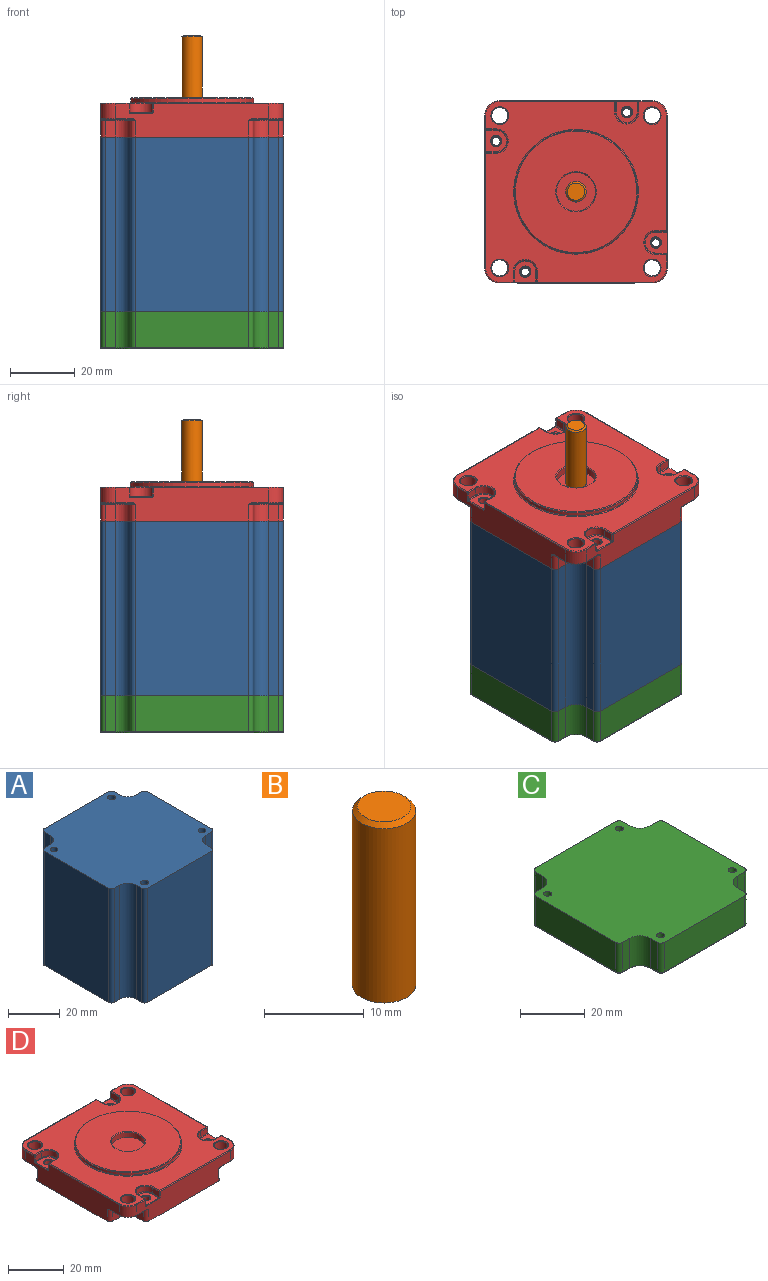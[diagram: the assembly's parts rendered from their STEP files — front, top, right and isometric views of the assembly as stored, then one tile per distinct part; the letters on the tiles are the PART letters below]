
ASSEMBLY  parts=4 mates=3
PART A: 30 faces, bbox 56.4x56.4x54 mm
  f0: cylinder r=1.5mm len=54mm, axis (0,0,1), area 508.9mm2, adj f8,f9
  f1: cylinder r=1.5mm len=54mm, axis (0,0,1), area 508.9mm2, adj f8,f9
  f2: cylinder r=1.5mm len=54mm, axis (0,0,1), area 508.9mm2, adj f8,f9
  f3: cylinder r=1.5mm len=54mm, axis (0,0,1), area 508.9mm2, adj f8,f9
  f4: plane 54x35.14mm, normal (0,-1,0), area 1897.6mm2, adj f8,f9,f25,f26
  f5: plane 54x35.14mm, normal (-1,0,0), area 1897.6mm2, adj f8,f9,f23,f24
  f6: plane 54x35.14mm, normal (0,1,0), area 1897.6mm2, adj f8,f9,f22,f29
  f7: plane 54x35.14mm, normal (1,0,0), area 1897.6mm2, adj f8,f9,f27,f28
  f8: plane 56.4x56.4mm, normal (0,0,-1), area 2832.8mm2, adj f0,f1,f2,f3,f4,f5,f6,f7
  f9: plane 56.4x56.4mm, normal (0,0,1), area 2832.8mm2, adj f0,f1,f2,f3,f4,f5,f6,f7
  f10: plane 54x3.13mm, normal (0,1,0), area 169mm2, adj f8,f9,f12,f28
  f11: plane 54x3.13mm, normal (1,0,0), area 169mm2, adj f8,f9,f12,f29
  f12: cylinder r=4.5mm len=54mm, axis (0,0,1), area 381.7mm2, adj f8,f9,f10,f11
  f13: plane 54x3.13mm, normal (-1,0,0), area 169mm2, adj f8,f9,f14,f22
  f14: cylinder r=4.5mm len=54mm, axis (0,0,1), area 381.7mm2, adj f8,f9,f13,f15
  f15: plane 54x3.13mm, normal (0,1,0), area 169mm2, adj f8,f9,f14,f23
  f16: plane 54x3.13mm, normal (0,-1,0), area 169mm2, adj f8,f9,f17,f24
  f17: cylinder r=4.5mm len=54mm, axis (0,0,1), area 381.7mm2, adj f8,f9,f16,f18
  f18: plane 54x3.13mm, normal (-1,0,0), area 169mm2, adj f8,f9,f17,f25
  f19: cylinder r=4.5mm len=54mm, axis (0,0,1), area 381.7mm2, adj f8,f9,f20,f21
  f20: plane 54x3.13mm, normal (0,-1,0), area 169mm2, adj f8,f9,f19,f27
  f21: plane 54x3.13mm, normal (1,0,0), area 169mm2, adj f8,f9,f19,f26
  f22: cylinder r=1.5mm len=54mm, axis (0,0,1), area 127.2mm2, adj f6,f8,f9,f13
  f23: cylinder r=1.5mm len=54mm, axis (0,0,-1), area 127.2mm2, adj f5,f8,f9,f15
  f24: cylinder r=1.5mm len=54mm, axis (0,0,1), area 127.2mm2, adj f5,f8,f9,f16
  f25: cylinder r=1.5mm len=54mm, axis (0,0,-1), area 127.2mm2, adj f4,f8,f9,f18
  f26: cylinder r=1.5mm len=54mm, axis (0,0,1), area 127.2mm2, adj f4,f8,f9,f21
  f27: cylinder r=1.5mm len=54mm, axis (0,0,-1), area 127.2mm2, adj f7,f8,f9,f20
  f28: cylinder r=1.5mm len=54mm, axis (0,0,1), area 127.2mm2, adj f7,f8,f9,f10
  f29: cylinder r=1.5mm len=54mm, axis (0,0,-1), area 127.2mm2, adj f6,f8,f9,f11
PART B: 4 faces, bbox 6.4x6.4x21.9 mm
  f0: cone r=2.67mm half-angle=45deg, axis (0,0,-1), area 13mm2, adj f1,f2
  f1: cylinder r=3.17mm len=21.4mm, axis (0,0,-1), area 426.9mm2, adj f0,f3
  f2: plane 5.35x5.35mm, normal (0,0,1), area 22.5mm2, adj f0
  f3: plane 6.35x6.35mm, normal (0,0,-1), area 31.7mm2, adj f1
PART C: 61 faces, bbox 56.6x56.6x11.5 mm
  f0: cone r=6mm half-angle=45deg, axis (0,0,-1), area 13.6mm2, adj f9,f14
  f1: cone r=1.25mm half-angle=45deg, axis (0,0,-1), area 6.7mm2, adj f2,f14
  f2: cylinder r=1.25mm len=11mm, axis (0,0,1), area 86.4mm2, adj f1,f15
  f3: cone r=1.25mm half-angle=45deg, axis (0,0,-1), area 6.7mm2, adj f4,f14
  f4: cylinder r=1.25mm len=11mm, axis (0,0,1), area 86.4mm2, adj f3,f15
  f5: cone r=1.25mm half-angle=45deg, axis (0,0,-1), area 6.7mm2, adj f6,f14
  f6: cylinder r=1.25mm len=11mm, axis (0,0,1), area 86.4mm2, adj f5,f15
  f7: cone r=1.25mm half-angle=45deg, axis (0,0,-1), area 6.7mm2, adj f8,f14
  f8: cylinder r=1.25mm len=11mm, axis (0,0,1), area 86.4mm2, adj f7,f15
  f9: cylinder r=6mm len=12mm, axis (0,0,-1), area 141.4mm2, adj f0,f16
  f10: plane 35.14x11.25mm, normal (1,0,0), area 395.3mm2, adj f15,f34,f35,f56
  f11: plane 35.14x11.25mm, normal (0,-1,0), area 395.3mm2, adj f15,f32,f33,f44
  f12: plane 35.14x11.25mm, normal (-1,0,0), area 395.3mm2, adj f15,f30,f31,f41
  f13: plane 35.14x11.25mm, normal (0,1,0), area 395.3mm2, adj f15,f29,f36,f53
  f14: plane 55.9x55.9mm, normal (0,0,-1), area 2646.9mm2, adj f0,f1,f3,f5,f7,f37,f38,f39
  f15: plane 56.4x56.4mm, normal (0,0,1), area 2841.4mm2, adj f2,f4,f6,f8,f10,f11,f12,f13
  f16: plane 12x12mm, normal (0,0,-1), area 113.1mm2, adj f9
  f17: plane 11.25x3.13mm, normal (0,1,0), area 35.2mm2, adj f15,f19,f35,f60
  f18: plane 11.25x3.13mm, normal (1,0,0), area 35.2mm2, adj f15,f19,f36,f57
  f19: cylinder r=4.5mm len=11.25mm, axis (0,0,1), area 79.5mm2, adj f15,f17,f18,f59
  f20: plane 11.25x3.13mm, normal (-1,0,0), area 35.2mm2, adj f15,f21,f29,f49
  f21: cylinder r=4.5mm len=11.25mm, axis (0,0,1), area 79.5mm2, adj f15,f20,f22,f47
  f22: plane 11.25x3.13mm, normal (0,1,0), area 35.2mm2, adj f15,f21,f30,f45
  f23: plane 11.25x3.13mm, normal (0,-1,0), area 35.2mm2, adj f15,f24,f31,f37
  f24: cylinder r=4.5mm len=11.25mm, axis (0,0,1), area 79.5mm2, adj f15,f23,f25,f38
  f25: plane 11.25x3.13mm, normal (-1,0,0), area 35.2mm2, adj f15,f24,f32,f40
  f26: plane 11.25x3.13mm, normal (0,-1,0), area 35.2mm2, adj f15,f27,f34,f52
  f27: cylinder r=4.5mm len=11.25mm, axis (0,0,1), area 79.5mm2, adj f15,f26,f28,f50
  f28: plane 11.25x3.13mm, normal (1,0,0), area 35.2mm2, adj f15,f27,f33,f48
  f29: cylinder r=1.5mm len=11.25mm, axis (0,0,1), area 26.5mm2, adj f13,f15,f20,f51
  f30: cylinder r=1.5mm len=11.25mm, axis (0,0,-1), area 26.5mm2, adj f12,f15,f22,f43
  f31: cylinder r=1.5mm len=11.25mm, axis (0,0,1), area 26.5mm2, adj f12,f15,f23,f39
  f32: cylinder r=1.5mm len=11.25mm, axis (0,0,-1), area 26.5mm2, adj f11,f15,f25,f42
  f33: cylinder r=1.5mm len=11.25mm, axis (0,0,1), area 26.5mm2, adj f11,f15,f28,f46
  f34: cylinder r=1.5mm len=11.25mm, axis (0,0,-1), area 26.5mm2, adj f10,f15,f26,f54
  f35: cylinder r=1.5mm len=11.25mm, axis (0,0,1), area 26.5mm2, adj f10,f15,f17,f58
  f36: cylinder r=1.5mm len=11.25mm, axis (0,0,-1), area 26.5mm2, adj f13,f15,f18,f55
  f37: cylinder r=0.25mm len=3.13mm, axis (1,0,0), area 1.2mm2, adj f14,f23,f38,f39
  f38: torus R=4.75mm, axis (0,0,-1), area 2.8mm2, adj f14,f24,f37,f40
  f39: torus R=1.25mm, axis (0,0,-1), area 0.9mm2, adj f14,f31,f37,f41
  f40: cylinder r=0.25mm len=3.13mm, axis (0,-1,0), area 1.2mm2, adj f14,f25,f38,f42
  f41: cylinder r=0.25mm len=35.14mm, axis (0,-1,0), area 13.8mm2, adj f12,f14,f39,f43
  f42: torus R=1.25mm, axis (0,0,-1), area 0.9mm2, adj f14,f32,f40,f44
  f43: torus R=1.25mm, axis (0,0,-1), area 0.9mm2, adj f14,f30,f41,f45
  f44: cylinder r=0.25mm len=35.14mm, axis (1,0,0), area 13.8mm2, adj f11,f14,f42,f46
  f45: cylinder r=0.25mm len=3.13mm, axis (-1,0,0), area 1.2mm2, adj f14,f22,f43,f47
  f46: torus R=1.25mm, axis (0,0,-1), area 0.9mm2, adj f14,f33,f44,f48
  f47: torus R=4.75mm, axis (0,0,-1), area 2.8mm2, adj f14,f21,f45,f49
  f48: cylinder r=0.25mm len=3.13mm, axis (0,1,0), area 1.2mm2, adj f14,f28,f46,f50
  f49: cylinder r=0.25mm len=3.13mm, axis (0,-1,0), area 1.2mm2, adj f14,f20,f47,f51
  f50: torus R=4.75mm, axis (0,0,-1), area 2.8mm2, adj f14,f27,f48,f52
  f51: torus R=1.25mm, axis (0,0,-1), area 0.9mm2, adj f14,f29,f49,f53
  f52: cylinder r=0.25mm len=3.13mm, axis (1,0,0), area 1.2mm2, adj f14,f26,f50,f54
  f53: cylinder r=0.25mm len=35.14mm, axis (-1,0,0), area 13.8mm2, adj f13,f14,f51,f55
  f54: torus R=1.25mm, axis (0,0,-1), area 0.9mm2, adj f14,f34,f52,f56
  f55: torus R=1.25mm, axis (0,0,-1), area 0.9mm2, adj f14,f36,f53,f57
  f56: cylinder r=0.25mm len=35.14mm, axis (0,1,0), area 13.8mm2, adj f10,f14,f54,f58
  f57: cylinder r=0.25mm len=3.13mm, axis (0,1,0), area 1.2mm2, adj f14,f18,f55,f59
  f58: torus R=1.25mm, axis (0,0,-1), area 0.9mm2, adj f14,f35,f56,f60
  f59: torus R=4.75mm, axis (0,0,-1), area 2.8mm2, adj f14,f19,f57,f60
  f60: cylinder r=0.25mm len=3.13mm, axis (-1,0,0), area 1.2mm2, adj f14,f17,f58,f59
PART D: 174 faces, bbox 57.8x57.8x12.3 mm
  f0: cone r=6mm half-angle=45deg, axis (0,0,1), area 13.6mm2, adj f26,f34
  f1: cone r=18.8mm half-angle=45deg, axis (0,0,-1), area 42mm2, adj f27,f34
  f2: torus R=19.3mm, axis (0,0,1), area 47.2mm2, adj f27,f33
  f3: torus R=2.75mm, axis (0,0,1), area 6.4mm2, adj f18,f55
  f4: torus R=2.75mm, axis (0,0,1), area 6.4mm2, adj f20,f63
  f5: torus R=2.75mm, axis (0,0,1), area 6.4mm2, adj f24,f59
  f6: torus R=2.75mm, axis (0,0,1), area 6.4mm2, adj f22,f68
  f7: torus R=3.75mm, axis (0,0,1), area 4.4mm2, adj f25,f33,f98,f104
  f8: torus R=3.25mm, axis (0,0,1), area 4.2mm2, adj f25,f38,f85,f97
  f9: cone r=1.75mm half-angle=45deg, axis (0,0,1), area 3.6mm2, adj f10,f50
  f10: cylinder r=1.5mm len=7.25mm, axis (0,0,1), area 68.3mm2, adj f9,f32
  f11: cone r=1.75mm half-angle=45deg, axis (0,0,1), area 3.6mm2, adj f12,f38
  f12: cylinder r=1.5mm len=7.25mm, axis (0,0,1), area 68.3mm2, adj f11,f32
  f13: cone r=1.75mm half-angle=45deg, axis (0,0,1), area 3.6mm2, adj f14,f42
  f14: cylinder r=1.5mm len=7.25mm, axis (0,0,1), area 68.3mm2, adj f13,f32
  f15: cone r=1.75mm half-angle=45deg, axis (0,0,1), area 3.6mm2, adj f16,f46
  f16: cylinder r=1.5mm len=7.25mm, axis (0,0,1), area 68.3mm2, adj f15,f32
  f17: cone r=2.75mm half-angle=45deg, axis (0,0,1), area 5.8mm2, adj f18,f33
  f18: cylinder r=2.5mm len=5mm, axis (0,0,1), area 70.7mm2, adj f3,f17
  f19: cone r=2.75mm half-angle=45deg, axis (0,0,1), area 5.8mm2, adj f20,f33
  f20: cylinder r=2.5mm len=5mm, axis (0,0,1), area 70.7mm2, adj f4,f19
  f21: cone r=2.75mm half-angle=45deg, axis (0,0,1), area 5.8mm2, adj f22,f33
  f22: cylinder r=2.5mm len=5mm, axis (0,0,1), area 70.7mm2, adj f6,f21
  f23: cone r=2.75mm half-angle=45deg, axis (0,0,1), area 5.8mm2, adj f24,f33
  f24: cylinder r=2.5mm len=5mm, axis (0,0,1), area 70.7mm2, adj f5,f23
  f25: cylinder r=3.5mm len=7mm, axis (0,0,1), area 27.5mm2, adj f7,f8,f36,f37
  f26: cylinder r=6mm len=12mm, axis (0,0,1), area 84.8mm2, adj f0,f35
  f27: cylinder r=19.05mm len=38.1mm, axis (0,0,-1), area 131.7mm2, adj f1,f2
  f28: plane 47.61x10.46mm, normal (1,0,0), area 396.6mm2, adj f32,f44,f45,f46,f53,f54,f76,f77
  f29: plane 47.61x10.46mm, normal (0,-1,0), area 393.4mm2, adj f32,f51,f53,f74,f75,f112,f116,f120
  f30: plane 47.61x10.46mm, normal (-1,0,0), area 393.4mm2, adj f32,f51,f52,f72,f73,f87,f88,f92
  f31: plane 47.61x10.46mm, normal (0,1,0), area 393.4mm2, adj f32,f52,f54,f71,f78,f80,f81,f86
  f32: plane 56.4x56.4mm, normal (0,0,-1), area 2832.8mm2, adj f10,f12,f14,f16,f28,f29,f30,f31
  f33: plane 55.9x55.9mm, normal (0,0,1), area 1658.2mm2, adj f2,f7,f17,f19,f21,f23,f80,f82
  f34: plane 37.6x37.6mm, normal (0,0,1), area 987.6mm2, adj f0,f1
  f35: plane 12x12mm, normal (0,0,1), area 113.1mm2, adj f26
  f36: plane 3.25x2.5mm, normal (0,1,0), area 8.1mm2, adj f25,f97,f103,f104
  f37: plane 3.25x2.5mm, normal (0,-1,0), area 8.1mm2, adj f25,f85,f87,f98
  f38: plane 6.5x6.5mm, normal (0,0,1), area 28.1mm2, adj f8,f11,f85,f96,f97
  f39: cylinder r=3.5mm len=7mm, axis (0,0,1), area 27.5mm2, adj f40,f41,f121,f122
  f40: plane 3.25x2.5mm, normal (-1,0,0), area 8.1mm2, adj f39,f125,f126,f130
  f41: plane 3.25x2.5mm, normal (1,0,0), area 8.1mm2, adj f39,f116,f117,f118
  f42: plane 6.5x6.5mm, normal (0,0,1), area 28.1mm2, adj f13,f117,f121,f124,f125
  f43: cylinder r=3.5mm len=7mm, axis (0,0,1), area 27.5mm2, adj f44,f45,f113,f132
  f44: plane 3.5x2.5mm, normal (0,-1,0), area 8.7mm2, adj f28,f43,f111,f133
  f45: plane 3.5x2.5mm, normal (0,1,0), area 8.7mm2, adj f28,f43,f115,f131
  f46: plane 6.75x6.5mm, normal (0,0,1), area 29.7mm2, adj f15,f28,f131,f132,f133
  f47: cylinder r=3.5mm len=7mm, axis (0,0,1), area 27.5mm2, adj f48,f49,f84,f94
  f48: plane 3.25x2.5mm, normal (1,0,0), area 8.1mm2, adj f47,f79,f81,f89
  f49: plane 3.25x2.5mm, normal (-1,0,0), area 8.1mm2, adj f47,f90,f99,f100
  f50: plane 6.5x6.5mm, normal (0,0,1), area 28.1mm2, adj f9,f79,f84,f90,f91
  f51: cylinder r=4.5mm len=4.5mm, axis (0,0,1), area 31.8mm2, adj f29,f30,f110,f138
  f52: cylinder r=4.5mm len=4.5mm, axis (0,0,1), area 31.8mm2, adj f30,f31,f82,f158
  f53: cylinder r=4.5mm len=4.5mm, axis (0,0,1), area 31.8mm2, adj f28,f29,f123,f148
  f54: cylinder r=4.5mm len=4.5mm, axis (0,0,1), area 31.8mm2, adj f28,f31,f107,f173
  f55: plane 9.16x9.16mm, normal (0,0,-1), area 43.4mm2, adj f3,f164,f165,f166,f167,f168,f171,f172
  f56: plane 5.25x3.13mm, normal (1,0,0), area 16.4mm2, adj f32,f58,f78,f165
  f57: plane 5.25x3.13mm, normal (0,1,0), area 16.4mm2, adj f32,f58,f77,f166
  f58: cylinder r=4.5mm len=5.25mm, axis (0,0,1), area 37.1mm2, adj f32,f56,f57,f164
  f59: plane 9.16x9.16mm, normal (0,0,-1), area 43.4mm2, adj f5,f145,f146,f147,f148,f149,f150,f151
  f60: plane 5.25x3.13mm, normal (1,0,0), area 16.4mm2, adj f32,f61,f75,f147
  f61: cylinder r=4.5mm len=5.25mm, axis (0,0,1), area 37.1mm2, adj f32,f60,f62,f149
  f62: plane 5.25x3.13mm, normal (0,-1,0), area 16.4mm2, adj f32,f61,f76,f151
  f63: plane 9.16x9.16mm, normal (0,0,-1), area 43.4mm2, adj f4,f155,f156,f157,f158,f159,f160,f161
  f64: plane 5.25x3.13mm, normal (-1,0,0), area 16.4mm2, adj f32,f65,f71,f157
  f65: cylinder r=4.5mm len=5.25mm, axis (0,0,1), area 37.1mm2, adj f32,f64,f66,f159
  f66: plane 5.25x3.13mm, normal (0,1,0), area 16.4mm2, adj f32,f65,f72,f161
  f67: cylinder r=4.5mm len=5.25mm, axis (0,0,1), area 37.1mm2, adj f32,f69,f70,f139
  f68: plane 9.16x9.16mm, normal (0,0,-1), area 43.4mm2, adj f6,f135,f136,f137,f138,f139,f140,f141
  f69: plane 5.25x3.13mm, normal (-1,0,0), area 16.4mm2, adj f32,f67,f74,f141
  f70: plane 5.25x3.13mm, normal (0,-1,0), area 16.4mm2, adj f32,f67,f73,f137
  f71: cylinder r=1.5mm len=5.25mm, axis (0,0,1), area 12.4mm2, adj f31,f32,f64,f155
  f72: cylinder r=1.5mm len=5.25mm, axis (0,0,-1), area 12.4mm2, adj f30,f32,f66,f163
  f73: cylinder r=1.5mm len=5.25mm, axis (0,0,1), area 12.4mm2, adj f30,f32,f70,f135
  f74: cylinder r=1.5mm len=5.25mm, axis (0,0,-1), area 12.4mm2, adj f29,f32,f69,f143
  f75: cylinder r=1.5mm len=5.25mm, axis (0,0,1), area 12.4mm2, adj f29,f32,f60,f145
  f76: cylinder r=1.5mm len=5.25mm, axis (0,0,-1), area 12.4mm2, adj f28,f32,f62,f153
  f77: cylinder r=1.5mm len=5.25mm, axis (0,0,1), area 12.4mm2, adj f28,f32,f57,f168
  f78: cylinder r=1.5mm len=5.25mm, axis (0,0,-1), area 12.4mm2, adj f31,f32,f56,f167
  f79: cylinder r=0.25mm len=3.25mm, axis (0,-1,0), area 1.3mm2, adj f48,f50,f84,f86
  f80: cylinder r=0.25mm len=35.65mm, axis (-1,0,0), area 14mm2, adj f31,f33,f82,f83
  f81: cylinder r=0.25mm len=2.5mm, axis (0,0,-1), area 1mm2, adj f31,f48,f83,f86
  f82: torus R=4.25mm, axis (0,0,1), area 2.7mm2, adj f33,f52,f80,f88
  f83: sphere r=0.25mm, area 0.1mm2, adj f80,f81,f89
  f84: torus R=3.25mm, axis (0,0,1), area 4.2mm2, adj f47,f50,f79,f90
  f85: cylinder r=0.25mm len=3.25mm, axis (-1,0,0), area 1.3mm2, adj f8,f37,f38,f92
  f86: torus R=0.5mm, axis (0,1,0), area 0.2mm2, adj f31,f79,f81,f91
  f87: cylinder r=0.25mm len=2.5mm, axis (0,0,1), area 1mm2, adj f30,f37,f92,f93
  f88: cylinder r=0.25mm len=4.25mm, axis (0,-1,0), area 1.7mm2, adj f30,f33,f82,f93
  f89: cylinder r=0.25mm len=3.25mm, axis (0,1,0), area 1.3mm2, adj f33,f48,f83,f94
  f90: cylinder r=0.25mm len=3.25mm, axis (0,1,0), area 1.3mm2, adj f49,f50,f84,f95
  f91: cylinder r=0.25mm len=6.5mm, axis (1,0,0), area 2.6mm2, adj f31,f50,f86,f95
  f92: torus R=0.5mm, axis (-1,0,0), area 0.2mm2, adj f30,f85,f87,f96
  f93: sphere r=0.25mm, area 0.1mm2, adj f87,f88,f98
  f94: torus R=3.75mm, axis (0,0,1), area 4.4mm2, adj f33,f47,f89,f99
  f95: torus R=0.5mm, axis (0,1,0), area 0.2mm2, adj f31,f90,f91,f100
  f96: cylinder r=0.25mm len=6.5mm, axis (0,1,0), area 2.6mm2, adj f30,f38,f92,f101
  f97: cylinder r=0.25mm len=3.25mm, axis (1,0,0), area 1.3mm2, adj f8,f36,f38,f101
  f98: cylinder r=0.25mm len=3.25mm, axis (1,0,0), area 1.3mm2, adj f7,f33,f37,f93
  f99: cylinder r=0.25mm len=3.25mm, axis (0,-1,0), area 1.3mm2, adj f33,f49,f94,f102
  f100: cylinder r=0.25mm len=2.5mm, axis (0,0,1), area 1mm2, adj f31,f49,f95,f102
  f101: torus R=0.5mm, axis (-1,0,0), area 0.2mm2, adj f30,f96,f97,f103
  f102: sphere r=0.25mm, area 0.1mm2, adj f99,f100,f105
  f103: cylinder r=0.25mm len=2.5mm, axis (0,0,-1), area 1mm2, adj f30,f36,f101,f106
  f104: cylinder r=0.25mm len=3.25mm, axis (-1,0,0), area 1.3mm2, adj f7,f33,f36,f106
  f105: cylinder r=0.25mm len=4.25mm, axis (-1,0,0), area 1.7mm2, adj f31,f33,f102,f107
  f106: sphere r=0.25mm, area 0.1mm2, adj f103,f104,f108
  f107: torus R=4.25mm, axis (0,0,1), area 2.7mm2, adj f33,f54,f105,f109
  f108: cylinder r=0.25mm len=35.65mm, axis (0,-1,0), area 14mm2, adj f30,f33,f106,f110
  f109: cylinder r=0.25mm len=35.9mm, axis (0,1,0), area 14mm2, adj f28,f33,f107,f111
  f110: torus R=4.25mm, axis (0,0,1), area 2.7mm2, adj f33,f51,f108,f112
  f111: cylinder r=0.25mm len=3.5mm, axis (1,0,0), area 1.3mm2, adj f33,f44,f109,f113
  f112: cylinder r=0.25mm len=4.25mm, axis (1,0,0), area 1.7mm2, adj f29,f33,f110,f114
  f113: torus R=3.75mm, axis (0,0,1), area 4.4mm2, adj f33,f43,f111,f115
  f114: sphere r=0.25mm, area 0.1mm2, adj f112,f116,f118
  f115: cylinder r=0.25mm len=3.5mm, axis (-1,0,0), area 1.3mm2, adj f33,f45,f113,f119
  f116: cylinder r=0.25mm len=2.5mm, axis (0,0,1), area 1mm2, adj f29,f41,f114,f120
  f117: cylinder r=0.25mm len=3.25mm, axis (0,-1,0), area 1.3mm2, adj f41,f42,f120,f121
  f118: cylinder r=0.25mm len=3.25mm, axis (0,1,0), area 1.3mm2, adj f33,f41,f114,f122
  f119: cylinder r=0.25mm len=4.5mm, axis (0,1,0), area 1.7mm2, adj f28,f33,f115,f123
  f120: torus R=0.5mm, axis (0,-1,0), area 0.2mm2, adj f29,f116,f117,f124
  f121: torus R=3.25mm, axis (0,0,1), area 4.2mm2, adj f39,f42,f117,f125
  f122: torus R=3.75mm, axis (0,0,1), area 4.4mm2, adj f33,f39,f118,f126
  f123: torus R=4.25mm, axis (0,0,1), area 2.7mm2, adj f33,f53,f119,f127
  f124: cylinder r=0.25mm len=6.5mm, axis (-1,0,0), area 2.6mm2, adj f29,f42,f120,f128
  f125: cylinder r=0.25mm len=3.25mm, axis (0,1,0), area 1.3mm2, adj f40,f42,f121,f128
  f126: cylinder r=0.25mm len=3.25mm, axis (0,-1,0), area 1.3mm2, adj f33,f40,f122,f129
  f127: cylinder r=0.25mm len=35.65mm, axis (1,0,0), area 14mm2, adj f29,f33,f123,f129
  f128: torus R=0.5mm, axis (0,-1,0), area 0.2mm2, adj f29,f124,f125,f130
  f129: sphere r=0.25mm, area 0.1mm2, adj f126,f127,f130
  f130: cylinder r=0.25mm len=2.5mm, axis (0,0,-1), area 1mm2, adj f29,f40,f128,f129
  f131: cylinder r=0.25mm len=3.5mm, axis (1,0,0), area 1.4mm2, adj f28,f45,f46,f132
  f132: torus R=3.25mm, axis (0,0,1), area 4.2mm2, adj f43,f46,f131,f133
  f133: cylinder r=0.25mm len=3.5mm, axis (-1,0,0), area 1.4mm2, adj f28,f44,f46,f132
  f134: bspline ~1.22x0.5mm, area 0.2mm2, adj f30,f135,f136
  f135: torus R=1.75mm, axis (0,0,1), area 0.7mm2, adj f68,f73,f134,f137
  f136: cylinder r=0.25mm len=4.91mm, axis (0,-1,0), area 1.9mm2, adj f30,f68,f134,f138
  f137: cylinder r=0.25mm len=3.13mm, axis (1,0,0), area 1.2mm2, adj f68,f70,f135,f139
  f138: torus R=4.25mm, axis (0,0,1), area 2.7mm2, adj f51,f68,f136,f140
  f139: torus R=4.25mm, axis (0,0,1), area 2.7mm2, adj f67,f68,f137,f141
  f140: cylinder r=0.25mm len=4.91mm, axis (1,0,0), area 1.9mm2, adj f29,f68,f138,f142
  f141: cylinder r=0.25mm len=3.13mm, axis (0,-1,0), area 1.2mm2, adj f68,f69,f139,f143
  f142: bspline ~1.22x0.5mm, area 0.2mm2, adj f29,f140,f143
  f143: torus R=1.75mm, axis (0,0,1), area 0.7mm2, adj f68,f74,f141,f142
  f144: bspline ~1.22x0.5mm, area 0.2mm2, adj f29,f145,f146
  f145: torus R=1.75mm, axis (0,0,1), area 0.7mm2, adj f59,f75,f144,f147
  f146: cylinder r=0.25mm len=4.91mm, axis (1,0,0), area 1.9mm2, adj f29,f59,f144,f148
  f147: cylinder r=0.25mm len=3.13mm, axis (0,1,0), area 1.2mm2, adj f59,f60,f145,f149
  f148: torus R=4.25mm, axis (0,0,1), area 2.7mm2, adj f53,f59,f146,f150
  f149: torus R=4.25mm, axis (0,0,1), area 2.7mm2, adj f59,f61,f147,f151
  f150: cylinder r=0.25mm len=4.91mm, axis (0,1,0), area 1.9mm2, adj f28,f59,f148,f152
  f151: cylinder r=0.25mm len=3.13mm, axis (1,0,0), area 1.2mm2, adj f59,f62,f149,f153
  f152: bspline ~1.22x0.5mm, area 0.2mm2, adj f28,f150,f153
  f153: torus R=1.75mm, axis (0,0,1), area 0.7mm2, adj f59,f76,f151,f152
  f154: bspline ~1.22x0.5mm, area 0.2mm2, adj f31,f155,f156
  f155: torus R=1.75mm, axis (0,0,1), area 0.7mm2, adj f63,f71,f154,f157
  f156: cylinder r=0.25mm len=4.91mm, axis (-1,0,0), area 1.9mm2, adj f31,f63,f154,f158
  f157: cylinder r=0.25mm len=3.13mm, axis (0,-1,0), area 1.2mm2, adj f63,f64,f155,f159
  f158: torus R=4.25mm, axis (0,0,1), area 2.7mm2, adj f52,f63,f156,f160
  f159: torus R=4.25mm, axis (0,0,1), area 2.7mm2, adj f63,f65,f157,f161
  f160: cylinder r=0.25mm len=4.91mm, axis (0,-1,0), area 1.9mm2, adj f30,f63,f158,f162
  f161: cylinder r=0.25mm len=3.13mm, axis (-1,0,0), area 1.2mm2, adj f63,f66,f159,f163
  f162: bspline ~1.22x0.5mm, area 0.2mm2, adj f30,f160,f163
  f163: torus R=1.75mm, axis (0,0,1), area 0.7mm2, adj f63,f72,f161,f162
  f164: torus R=4.25mm, axis (0,0,1), area 2.7mm2, adj f55,f58,f165,f166
  f165: cylinder r=0.25mm len=3.13mm, axis (0,1,0), area 1.2mm2, adj f55,f56,f164,f167
  f166: cylinder r=0.25mm len=3.13mm, axis (-1,0,0), area 1.2mm2, adj f55,f57,f164,f168
  f167: torus R=1.75mm, axis (0,0,1), area 0.7mm2, adj f55,f78,f165,f169
  f168: torus R=1.75mm, axis (0,0,1), area 0.7mm2, adj f55,f77,f166,f170
  f169: bspline ~1.22x0.5mm, area 0.2mm2, adj f31,f167,f171
  f170: bspline ~1.22x0.5mm, area 0.2mm2, adj f28,f168,f172
  f171: cylinder r=0.25mm len=4.91mm, axis (-1,0,0), area 1.9mm2, adj f31,f55,f169,f173
  f172: cylinder r=0.25mm len=4.91mm, axis (0,1,0), area 1.9mm2, adj f28,f55,f170,f173
  f173: torus R=4.25mm, axis (0,0,1), area 2.7mm2, adj f54,f55,f171,f172
PLACE A t=(35.72,-70.36,14.7)mm
PLACE B t=(35.72,-70.36,14.7)mm
PLACE C t=(35.72,-70.36,14.7)mm
PLACE D t=(35.72,-70.36,14.7)mm
MATE fastened D.f0 <-> B.f0  axis (0,0,1) through (35.72,-70.36,13.8)mm
MATE fastened A.f1 <-> D.f7  axis (0,0,1) through (11.02,-54.66,4.2)mm
MATE fastened C.f3 <-> A.f1  axis (0,0,1) through (11.02,-54.66,-49.8)mm
